# Revit family: Legrand-Ups-Trimod_HE-10_80kVA
name_source: partatom
category: Installations électriques
revit_build: Autodesk Revit 2018 (Build: 20170223_1515(x64)
units: mm (PartAtom-declared; Revit-internal decimal feet)

## family parameters
Basée sur le plan de construction = Non
Conserver l'orientation des annotations = Non
Cote de connecteur circulaire = Utiliser le diamètre
Couper avec des vides une fois chargée = Non
Numéro OmniClass = 23.80.10.17.34
Partagée = Non
Point de calcul de pièce = Non
Titre OmniClass = Static Uninterruptible Power Supplies
Toujours verticalement = Oui
Type d'élément = Normal

## types (39) — shared parameters
Back Clearance = 100 mm  [stored 0.328084 ft]
Cabinet Depth = 628 mm  [stored 2.06037 ft]
Cabinet Width = 414 mm  [stored 1.35827 ft]
Conductors = Cables
Connection constraint = Ahead and bottom
Connection constraint (signal) = Behind and above
Fabricant = LEGRAND
Frequency of use = 50 Hz or 60 Hz selectable
Front Clearance = 1000 mm  [stored 3.28084 ft]
General Conditions of Use = https://export.legrand.com
Humidity = 0-95% not condensing
Installation type = On the floor
Modèle = TRIMOD HE
Operating altitude = up to 1000 m altitude without derating
Operating temperature = from 0°C to +40°C
Output power factor = 1
Side Clearance = 200 mm  [stored 0.656168 ft]
URL = https://ups.legrand.com
Visibilità aree d'installazione = Oui

## per-type parameters (varying)
| type | Active power of use | Cabinet Height | Input / Output phase configuration | Installation space | Max number of PM (N° x kW) | Max number of battery drawer (N°block - Ah) | Max sound pressure level | Nominal Power | Number of installed PM (N° x kW) | Number of installed battry (N°block - Ah) | Output Voltage | Weight |
| LG-310442 | 10 kW | 1370 mm | 1ph+N+PE/1ph+N+PE 3ph+N+PE/1ph+N+PE  1ph+N+PE/3ph+N+PE 3ph+N+PE/3ph+N+PE | 0.35 m³ |  | 3 string of 4 drawers (5 pcs 12V 7,2Ah) | < 46 dB at 1m | 10 kVA | 3 x 3,4 kW | 1 string of 4 drawers (5 pcs 12V 9Ah) | 220,230,240 Vac /380,400,415 Vac | 167.0 kg |
| LG-310443 | 10 kW | 1370 mm | 1ph+N+PE/1ph+N+PE 3ph+N+PE/1ph+N+PE  1ph+N+PE/3ph+N+PE 3ph+N+PE/3ph+N+PE | 0.35 m³ |  | 3 string of 4 drawers (5 pcs 12V 7,2Ah) | < 46 dB at 1m | 10 kVA | 3 x 3,4 kW | 2 string of 4 drawers (5 pcs 12V 7,2Ah) | 220,230,240 Vac /380,400,415 Vac | 223.0 kg |
| LG-310444 | 10 kW | 1370 mm | 1ph+N+PE/1ph+N+PE 3ph+N+PE/1ph+N+PE  1ph+N+PE/3ph+N+PE 3ph+N+PE/3ph+N+PE | 0.35 m³ |  | 3 string of 4 drawers (5 pcs 12V 7,2Ah) | < 46 dB at 1m | 10 kVA | 3 x 3,4 kW | 3 string of 4 drawers (5 pcs 12V 9Ah) | 220,230,240 Vac /380,400,415 Vac | 279.0 kg |
| LG-310402 | 10 kW | 1650 mm  [stored 5.41339 ft] | 1ph+N+PE/1ph+N+PE 3ph+N+PE/1ph+N+PE  1ph+N+PE/3ph+N+PE 3ph+N+PE/3ph+N+PE | 0.42 m³ |  | 4 string of 4 drawers (5 pcs 12V 7,2Ah) | < 46 dB at 1m | 10 kVA | 3 x 3,4 kW | 4 string of 4 drawers (5 pcs 12V 7,2Ah) | 220,230,240 Vac /380,400,415 Vac | 350.0 kg |
| LG-310445 | 15 kW | 1370 mm | 1ph+N+PE/1ph+N+PE 3ph+N+PE/1ph+N+PE  1ph+N+PE/3ph+N+PE 3ph+N+PE/3ph+N+PE | 0.35 m³ |  | 3 string of 4 drawers (5 pcs 12V 7,2Ah) | < 46 dB at 1m | 15 kVA | 3 x 5 kW | 1 string of 4 drawers (5 pcs 12V 9Ah) | 220,230,240 Vac /380,400,415 Vac | 220.0 kg |
| LG-310446 | 15 kW | 1370 mm | 1ph+N+PE/1ph+N+PE 3ph+N+PE/1ph+N+PE  1ph+N+PE/3ph+N+PE 3ph+N+PE/3ph+N+PE | 0.35 m³ |  | 3 string of 4 drawers (5 pcs 12V 9Ah) | < 46 dB at 1m | 15 kVA | 3 x 5 kW | 2 string of 4 drawers (5 pcs 12V 9Ah) | 220,230,240 Vac /380,400,415 Vac | 279.0 kg |
| LG-310407 | 15 kW | 1650 mm  [stored 5.41339 ft] | 1ph+N+PE/1ph+N+PE 3ph+N+PE/1ph+N+PE  1ph+N+PE/3ph+N+PE 3ph+N+PE/3ph+N+PE | 0.42 m³ |  | 4 string of 4 drawers (5 pcs 12V 9Ah) | < 46 dB at 1m | 15 kVA | 3 x 5 kW | 3 string of 4 drawers (5 pcs 12V 9Ah) | 220,230,240 Vac /380,400,415 Vac | 350.0 kg |
| LG-310447 | 20 kW | 1370 mm | 1ph+N+PE/1ph+N+PE 3ph+N+PE/1ph+N+PE  1ph+N+PE/3ph+N+PE 3ph+N+PE/3ph+N+PE | 0.35 m³ |  | 3 string of 4 drawers (5 pcs 12V 7,2Ah) | < 46 dB at 1m | 20 kVA | 3 x 6,7 kW | 1 string of 4 drawers (5 pcs 12V 9Ah) | 220,230,240 Vac /380,400,415 Vac | 220.0 kg |
| LG-310448 | 20 kW | 1370 mm | 1ph+N+PE/1ph+N+PE 3ph+N+PE/1ph+N+PE  1ph+N+PE/3ph+N+PE 3ph+N+PE/3ph+N+PE | 0.35 m³ |  | 3 string of 4 drawers (5 pcs 12V 7,2Ah) | < 46 dB at 1m | 20 kVA | 3 x 6,7 kW | 2 string of 4 drawers (5 pcs 12V 9Ah) | 220,230,240 Vac /380,400,415 Vac | 279.0 kg |
| LG-310413 | 20 kW | 1650 mm  [stored 5.41339 ft] | 1ph+N+PE/1ph+N+PE 3ph+N+PE/1ph+N+PE  1ph+N+PE/3ph+N+PE 3ph+N+PE/3ph+N+PE | 0.42 m³ |  | 4 string of 4 drawers (5 pcs 12V 9Ah) | < 46 dB at 1m | 20 kVA | 3 x 6,7 kW | 3 string of 4 drawers (5 pcs 12V 9Ah) | 220,230,240 Vac /380,400,415 Vac | 350.0 kg |
| LG-310417 | 30 kW | 1370 mm | 1ph+N+PE/1ph+N+PE 3ph+N+PE/1ph+N+PE  1ph+N+PE/3ph+N+PE 3ph+N+PE/3ph+N+PE | 0.35 m³ |  | 3 string of 4 drawers (5 pcs 12V 9Ah) | < 46 dB at 1m | 30 kVA | 6 x 5 kW | 3 string of 4 drawers (5 pcs 12V 9Ah) | 220,230,240 Vac /380,400,415 Vac | 325.0 kg |
| LG-310396 | 10 kW | 1370 mm | 1ph+N+PE/1ph+N+PE 3ph+N+PE/1ph+N+PE  1ph+N+PE/3ph+N+PE 3ph+N+PE/3ph+N+PE | 0.35 m³ |  | 3 string of 4 drawers (5 pcs 12V 7,2Ah) | < 46 dB at 1m | 10 kVA | 3 x 3,4 kW |  | 220,230,240 Vac /380,400,415 Vac | 120.0 kg |
| LG-310397 | 10 kW | 1650 mm  [stored 5.41339 ft] | 1ph+N+PE/1ph+N+PE 3ph+N+PE/1ph+N+PE  1ph+N+PE/3ph+N+PE 3ph+N+PE/3ph+N+PE | 0.42 m³ |  | 4 strings of 4 drawers (5 pcs 12V 7.2Ah) | < 46 dB at 1m | 10 kVA | 3 x 3,4 kW |  | 220,230,240 Vac /380,400,415 Vac | 155.0 kg |
| LG-310408 | 15 kW | 1370 mm | 1ph+N+PE/1ph+N+PE 3ph+N+PE/1ph+N+PE  1ph+N+PE/3ph+N+PE 3ph+N+PE/3ph+N+PE | 0.35 m³ |  | 3 strings of 4 drawers (5 pcs 12V 9Ah) | < 46 dB at 1m | 15 kVA | 3 x 3,4 kW |  | 220,230,240 Vac /380,400,415 Vac | 120.0 kg |
| LG-310403 | 15 kW | 1650 mm  [stored 5.41339 ft] | 1ph+N+PE/1ph+N+PE 3ph+N+PE/1ph+N+PE  1ph+N+PE/3ph+N+PE 3ph+N+PE/3ph+N+PE | 0.42 m³ |  | 4 strings of 4 drawers (5 pcs 12V 9Ah) | < 46 dB at 1m | 15 kVA | 3 x 5 kW |  | 220,230,240 Vac /380,400,415 Vac | 155.0 kg |
| LG-310414 | 20 kW | 1370 mm | 1ph+N+PE/1ph+N+PE 3ph+N+PE/1ph+N+PE  1ph+N+PE/3ph+N+PE 3ph+N+PE/3ph+N+PE | 0.35 m³ |  | 3 strings of 4 drawers (5 pcs 12V 9Ah) | < 46 dB at 1m | 20 kVA | 3 x 6,7 kW |  | 220,230,240 Vac /380,400,415 Vac | 120.0 kg |
| LG-310409 | 20 kW | 1650 mm  [stored 5.41339 ft] | 3ph+N+PE/3ph+N+PE | 0.42 m³ |  | 3 strings of 4 drawers (5 pcs 12V 9Ah) | < 46 dB at 1m | 20 kVA | 3 x 6,7 kW |  | 380,400,415 Vac | 155.0 kg |
| LG-310418 | 30 kW | 1370 mm | 1ph+N+PE/1ph+N+PE 3ph+N+PE/1ph+N+PE  1ph+N+PE/3ph+N+PE 3ph+N+PE/3ph+N+PE | 0.35 m³ |  |  | < 46 dB at 1m | 30 kVA | 6 x 5 kW |  | 220,230,240 Vac /380,400,415 Vac | 146.0 kg |
| LG-310415 | 30 kW | 1650 mm  [stored 5.41339 ft] | 3ph+N+PE/3ph+N+PE | 0.42 m³ |  | 3 strings of 4 drawers (5 pcs 12V 9Ah) | < 46 dB at 1m | 30 kVA | 6 x 5 kW |  | 380,400,415 Vac | 181.0 kg |
| LG-310419 | 40 kW | 1370 mm | 3ph+N+PE/3ph+N+PE | 0.35 m³ |  |  | < 46 dB at 1m | 40 kVA | 6 x 6,7 kW |  | 380,400,415 Vac | 146.0 kg |
| LG-310420 | 60 kW | 1370 mm | 3ph+N+PE/3ph+N+PE | 0.35 m³ |  |  | < 46 dB at 1m | 60 kVA | 9 x 6,7 kW |  | 380,400,415 Vac | 165.0 kg |
| LG-310422 | 0 kW | 1370 mm | 1ph+N+PE/1ph+N+PE 3ph+N+PE/1ph+N+PE  1ph+N+PE/3ph+N+PE 3ph+N+PE/3ph+N+PE | 0.35 m³ | 3 x 3,4 kW | 3 strings of 4 drawers (5 pcs 12V 7.2Ah) |  | 0 kVA |  |  | 220,230,240 Vac / 380,400,415 Vac | 85.0 kg |
| LG-310431 | 0 kW | 1650 mm  [stored 5.41339 ft] | 1ph+N+PE/1ph+N+PE 3ph+N+PE/1ph+N+PE  1ph+N+PE/3ph+N+PE 3ph+N+PE/3ph+N+PE | 0.42 m³ | 3 x 3,4 kW | 4 strings of 4 drawers (5 pcs 12V 7.2Ah) |  | 0 kVA |  |  | 220,230,240 Vac / 380,400,415 Vac | 98.0 kg |
| LG-310423 | 0 kW | 1370 mm | 1ph+N+PE/1ph+N+PE 3ph+N+PE/1ph+N+PE  1ph+N+PE/3ph+N+PE 3ph+N+PE/3ph+N+PE | 0.35 m³ | 3 x 5 or 6,7 kW | 3 strings of 4 drawers (5 pcs 12V 9Ah) |  | 0 kVA |  |  | 220,230,240 Vac / 380,400,415 Vac | 90.0 kg |
| LG-310432 | 0 kW | 1650 mm  [stored 5.41339 ft] | 1ph+N+PE/1ph+N+PE 3ph+N+PE/1ph+N+PE  1ph+N+PE/3ph+N+PE 3ph+N+PE/3ph+N+PE | 0.42 m³ | 3 x 5 or 6,7 kW | 3 strings of 4 drawers (5 pcs 12V 9Ah) |  | 0 kVA |  |  | 220,230,240 Vac / 380,400,415 Vac | 102.0 kg |
| LG-310433 | 0 kW | 1650 mm  [stored 5.41339 ft] | 1ph+N+PE/1ph+N+PE 3ph+N+PE/1ph+N+PE  1ph+N+PE/3ph+N+PE 3ph+N+PE/3ph+N+PE | 0.42 m³ | 3 x 5 or 6,7 kW | 4 strings of 4 drawers (5 pcs 12V 9Ah) |  | 0 kVA |  |  | 220,230,240 Vac / 380,400,415 Vac | 102.0 kg |
| LG-310424 | 0 kW | 1370 mm | 3ph+N+PE/3ph+N+PE | 0.35 m³ | 6 x 5 kW |  |  | 0 kVA |  |  | 220,230,240 Vac / 380,400,415 Vac | 80.0 kg |
| LG-310425 | 0 kW | 1370 mm | 1ph+N+PE/1ph+N+PE 3ph+N+PE/1ph+N+PE  1ph+N+PE/3ph+N+PE 3ph+N+PE/3ph+N+PE | 0.35 m³ | 6 x 5 kW |  |  | 0 kVA |  |  | 220,230,240 Vac / 380,400,415 Vac | 85.0 kg |
| LG-310434 | 0 kW | 1650 mm  [stored 5.41339 ft] | 3ph+N+PE/3ph+N+PE | 0.42 m³ | 6 x 5 kW | 3 strings of 4 drawers (5 pcs 12V 9Ah) |  | 0 kVA |  |  | 380,400,415 Vac | 104.0 kg |
| LG-310426 | 0 kW | 1370 mm | 3ph+N+PE/3ph+N+PE | 0.35 m³ | 6 x 6,7 kW |  |  | 0 kVA |  |  | 380,400,415 Vac | 80.0 kg |
| LG-310427 | 0 kW | 1370 mm | 3ph+N+PE/3ph+N+PE | 0.35 m³ | 9 x 6,7 kW |  |  | 0 kVA |  |  | 380,400,415 Vac | 90.0 kg |
| LG-310465 | 0 kW | 1370 mm | 1ph+N+PE/1ph+N+PE 3ph+N+PE/1ph+N+PE  1ph+N+PE/3ph+N+PE 3ph+N+PE/3ph+N+PE | 0.35 m³ | 3 x 3,4 kW | 3 strings of 4 drawers (5 pcs 12V 7,2 or 9Ah) | < 58-62 dB at 1m | 0 kVA |  |  | 220,230,240 Vac / 380,400,415 Vac | 86.0 kg |
| LG-310466 | 0 kW | 1370 mm | 1ph+N+PE/1ph+N+PE 3ph+N+PE/1ph+N+PE  1ph+N+PE/3ph+N+PE 3ph+N+PE/3ph+N+PE | 0.35 m³ | 3 x 5 or 6,7 kW | 3 strings of 4 drawers (5 pcs 12V 7,2 or 9Ah) | < 58-62 dB at 1m | 0 kVA |  |  | 220,230,240 Vac / 380,400,415 Vac | 89.0 kg |
| LG-310467 | 0 kW | 1650 mm  [stored 5.41339 ft] | 1ph+N+PE/1ph+N+PE 3ph+N+PE/1ph+N+PE  1ph+N+PE/3ph+N+PE 3ph+N+PE/3ph+N+PE | 0.42 m³ | 3 x 5 or 6,7 kW | 4 strings of 4 drawers (5 pcs 12V 7,2 or 9Ah) | < 58-62 dB at 1m | 0 kVA |  |  | 220,230,240 Vac / 380,400,415 Vac | 103.0 kg |
| LG-310468 | 0 kW | 1370 mm | 1ph+N+PE/1ph+N+PE 3ph+N+PE/1ph+N+PE  1ph+N+PE/3ph+N+PE 3ph+N+PE/3ph+N+PE | 0.35 m³ | 6 x 3,4 or 5 kW |  | < 58-62 dB at 1m | 0 kVA |  |  | 220,230,240 Vac / 380,400,415 Vac | 85.0 kg |
| LG-310469 | 0 kW | 1650 mm  [stored 5.41339 ft] | 3ph+N+PE/3ph+N+PE | 0.42 m³ | 6 x 5 kW | 3 strings of 4 drawers (5 pcs 12V 9Ah) | < 58-62 dB at 1m | 0 kVA |  |  | 380,400,415 Vac | 106.0 kg |
| LG-310471 | 0 kW | 1370 mm | 3ph+N+PE/3ph+N+PE | 0.35 m³ | 6 x 6,7 kW |  | < 58-62 dB at 1m | 0 kVA |  |  | 380,400,415 Vac | 82.0 kg |
| LG-310472 | 0 kW | 1370 mm | 3ph+N+PE/3ph+N+PE | 0.35 m³ | 9 x 6,7 kW |  | < 58-62 dB at 1m | 0 kVA |  |  | 380,400,415 Vac | 91.0 kg |
| LG-310473 | 0 kW | 1650 mm  [stored 5.41339 ft] | 3ph+N+PE/3ph+N+PE | 0.42 m³ | 12 x 6,7 kW |  | < 58-62 dB at 1m | 0 kVA |  |  | 380,400,415 Vac | 120.0 kg |

note: [stored X ft] marks values corroborated as IEEE doubles in the binary element streams (Revit-internal decimal feet)
